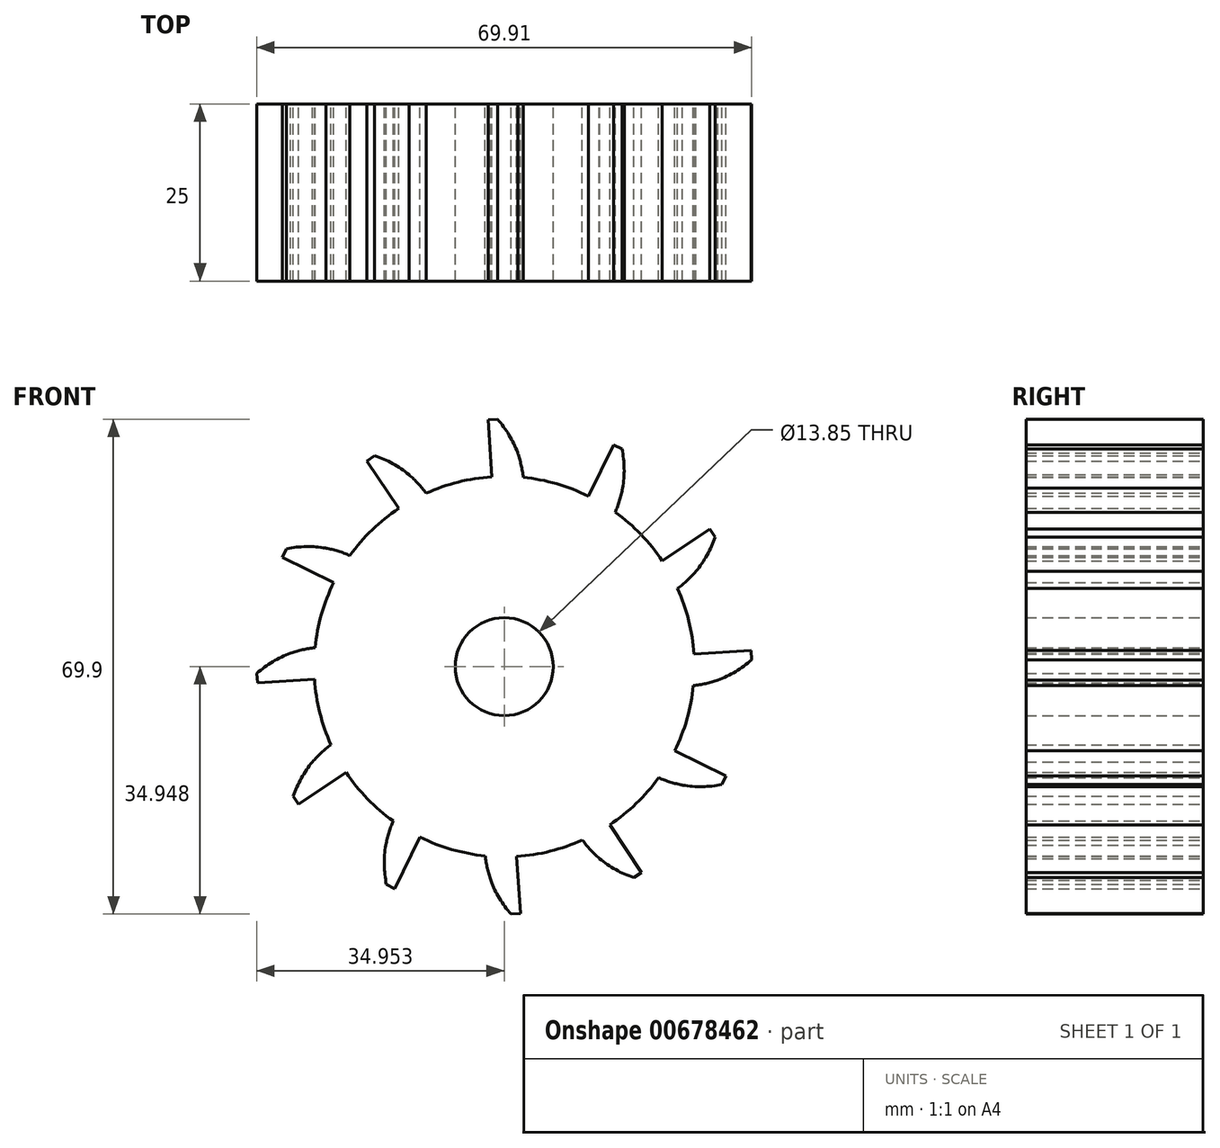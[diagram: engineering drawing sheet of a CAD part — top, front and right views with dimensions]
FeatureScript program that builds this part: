
annotation { "Feature Type Name" : "Feature", "Feature Type Description" : "" }
export const myFeature = defineFeature(function(context is Context, id is Id, definition is map)
    precondition{}
    {
        {
            var Q0;
            Q0=qCreatedBy(makeId("Front.planeOp"),FACE);
            var sketch = newSketch(context, id + "F0", { "sketchPlane" : qUnion([Q0])});
            skCircle(sketch, "E0", {"center": v(-10.5, 7.6) * mm, "radius": 26.86 * mm});
            skCircle(sketch, "E1", {"center": v(-10.5, 7.6) * mm, "radius": 31.75 * mm, "construction": true});
            skCircle(sketch, "E2", {"center": v(-10.5, 7.6) * mm, "radius": 28.19 * mm, "construction": true});
            skLineSegment(sketch, "E3", {"start": v(-10.5, 7.6) * mm, "end": v(-10.5, 128.63) * mm, "construction": true});
            skLineSegment(sketch, "E4", {"start": v(-10.5, 7.6) * mm, "end": v(-18.43, 128.63) * mm});
            skLineSegment(sketch, "E5", {"start": v(-10.5, 35.8) * mm, "end": v(-107.36, 35.8) * mm, "construction": true});
            skLineSegment(sketch, "E6", {"start": v(-10.5, 35.8) * mm, "end": v(-108.9, -0.02) * mm, "construction": true});
            skCircle(sketch, "E7", {"center": v(-10.5, 7.6) * mm, "radius": 26.49 * mm, "construction": true});
            skCircle(sketch, "E8", {"center": v(-10.5, 35.8) * mm, "radius": 7.3 * mm, "construction": true});
            skCircle(sketch, "E9", {"center": v(-17.36, 33.3) * mm, "radius": 7.3 * mm, "construction": true});
            skLineSegment(sketch, "E10", {"start": v(-13.13, 39.25) * mm, "end": v(-12.02, 39.32) * mm});
            skCircle(sketch, "E11", {"center": v(-10.5, 7.6) * mm, "radius": 21.96 * mm});
            skLineSegment(sketch, "E12", {"start": v(-12.85, 42.53) * mm, "end": v(-12.72, 42.54) * mm});
            skCircle(sketch, "E13", {"center": v(-10.5, 7.6) * mm, "radius": 6.93 * mm});
            skArc(sketch, "E14", {"start": v(-8.6, 37.8) * mm, "mid": v(-9.8, 40.31) * mm, "end": v(-11.45, 42.56) * mm});
            skArc(sketch, "E15", {"start": v(-7.8, 34.33) * mm, "mid": v(-8.11, 36.09) * mm, "end": v(-8.6, 37.8) * mm});
            skArc(sketch, "E16.MirrorCS", {"start": v(-16.32, 37.3) * mm, "mid": v(-15.45, 39.94) * mm, "end": v(-14.1, 42.39) * mm});
            skArc(sketch, "E17.MirrorCS", {"start": v(-16.65, 33.75) * mm, "mid": v(-16.58, 35.53) * mm, "end": v(-16.31, 37.3) * mm});
            skLineSegment(sketch, "E18", {"start": v(-14.1, 42.39) * mm, "end": v(-11.45, 42.56) * mm});
            skLineSegment(sketch, "E19", {"start": v(-16.31, 37.3) * mm, "end": v(-16.32, 37.3) * mm});
            skLineSegment(sketch, "E20", {"start": v(-8.6, 37.8) * mm, "end": v(-8.6, 37.8) * mm});
            skSolve(sketch);
        }
        {
            var Q0;
            Q0=makeQuery(id+"F0.imprint","IMPRINT",FACE,{"disambiguationData":[TD([[makeQuery(id+"F0.imprint","IMPRINT",EDGE,{"derivedFrom":sQuery(id+"F0.wireOp",EDGE,"E11")}),1.0]])]});
            var Q1;
            Q1=makeQuery(id+"F0.imprint","IMPRINT",FACE,{"disambiguationData":[TD([[makeQuery(id+"F0.imprint","IMPRINT",EDGE,{"derivedFrom":sQuery(id+"F0.wireOp",EDGE,"E0")}),1.0]])]});
            var Q2;
            {var subQ0=sQuery(id+"F0.wireOp",EDGE,"E16.MirrorCS");Q2=makeQuery(id+"F0.imprint","IMPRINT",FACE,{"disambiguationData":[TD([[makeQuery(id+"F0.imprint","IMPRINT",EDGE,{"derivedFrom":subQ0}),-1.0]])]});}
            var Q3;
            {var subQ0=sQuery(id+"F0.wireOp",EDGE,"E14");Q3=makeQuery(id+"F0.imprint","IMPRINT",FACE,{"disambiguationData":[TD([[makeQuery(id+"F0.imprint","IMPRINT",EDGE,{"derivedFrom":subQ0}),1.0]])]});}
            extrude(context, id + "F1", {"entities" : qUnion([Q0, Q1, Q2, Q3]), "depth" : 25 * mm, "offsetDistance" : 25 * mm});
        }
        {
            var Q0;
            Q0=makeQuery(id+"F1.opExtrude","SWEPT_BODY",BODY,{"disambiguationData":[OSD([sQuery(id+"F0.wireOp",EDGE,"E0"),sQuery(id+"F0.wireOp",EDGE,"E13"),sQuery(id+"F0.wireOp",EDGE,"E14"),sQuery(id+"F0.wireOp",EDGE,"E15"),sQuery(id+"F0.wireOp",EDGE,"E16.MirrorCS"),sQuery(id+"F0.wireOp",EDGE,"E17.MirrorCS"),sQuery(id+"F0.wireOp",EDGE,"E18"),sQuery(id+"F0.wireOp",EDGE,"E19"),sQuery(id+"F0.wireOp",EDGE,"E20")])]});
            var Q1;
            Q1=makeQuery(id+"F1.opExtrude","SWEPT_FACE",FACE,{"disambiguationData":[OSD([sQuery(id+"F0.wireOp",EDGE,"E0")])]});
            circularPattern(context, id + "F2", {"operationType" : NewBodyOperationType.ADD, "entities" : qUnion([Q0]), "axis" : qUnion([Q1]), "angle" : 360 * degree, "instanceCount" : 12, "equalSpace" : true});
        }
    });
